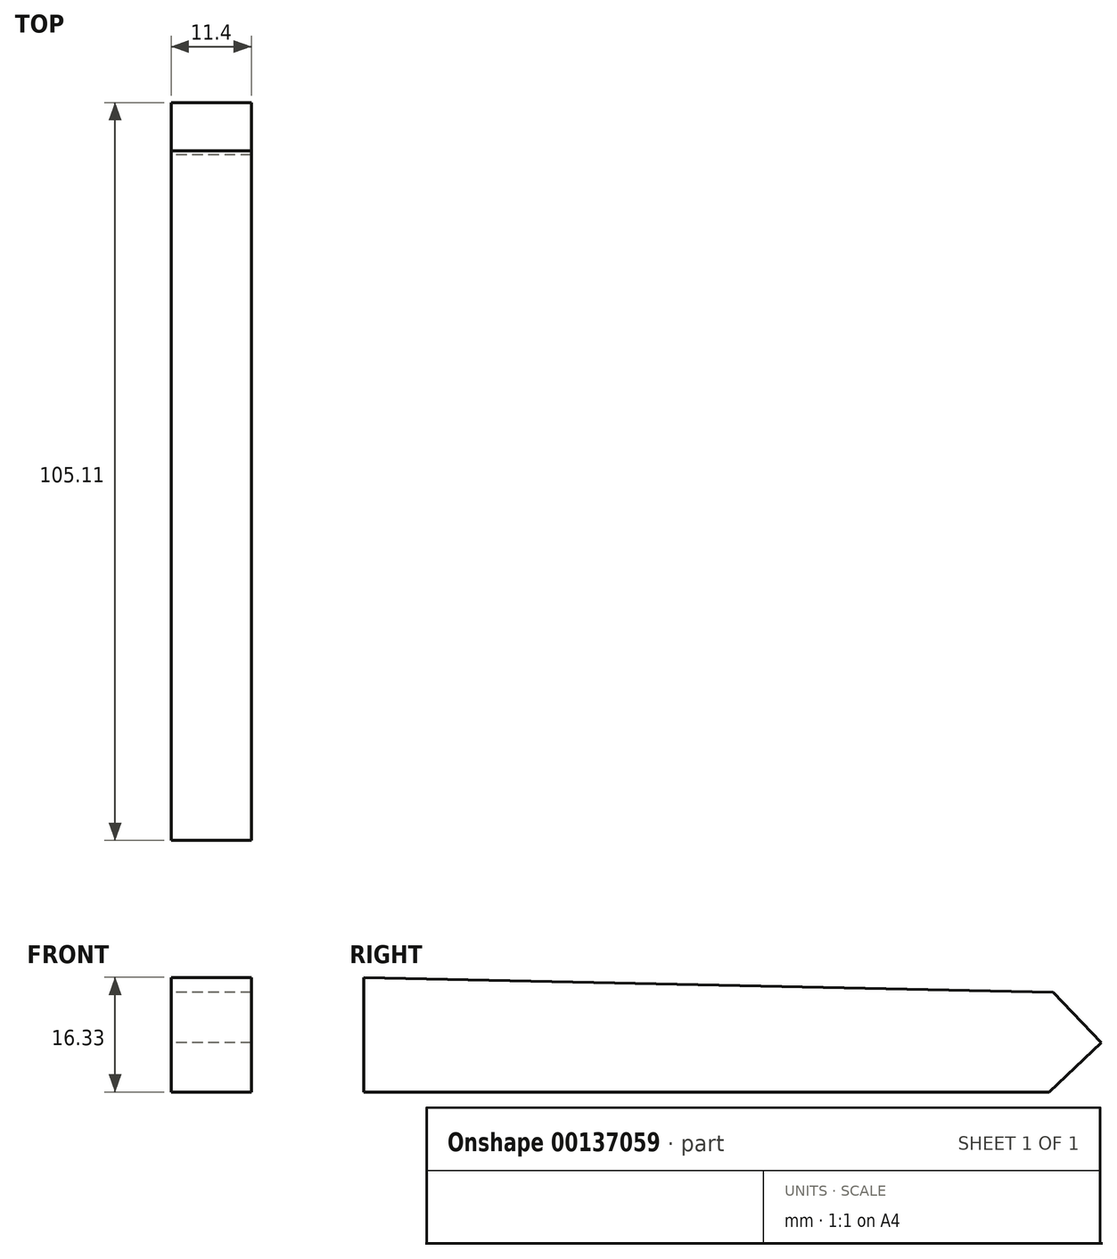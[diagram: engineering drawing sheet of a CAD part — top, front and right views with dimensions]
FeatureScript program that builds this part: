
annotation { "Feature Type Name" : "Feature", "Feature Type Description" : "" }
export const myFeature = defineFeature(function(context is Context, id is Id, definition is map)
    precondition{}
    {
        {
            var Q0;
            Q0=qCreatedBy(makeId("Right.planeOp"),FACE);
            var sketch = newSketch(context, id + "F0", { "sketchPlane" : qUnion([Q0])});
            skLineSegment(sketch, "E0", {"start": v(64.38, 7.22) * mm, "end": v(71.2, 0) * mm});
            skLineSegment(sketch, "E1", {"start": v(71.2, 0) * mm, "end": v(63.8, -7) * mm});
            skLineSegment(sketch, "E2", {"start": v(63.8, -7) * mm, "end": v(-33.9, -7) * mm});
            skLineSegment(sketch, "E3", {"start": v(-33.9, -7) * mm, "end": v(-33.9, 4.86) * mm});
            skLineSegment(sketch, "E4", {"start": v(-33.9, 4.86) * mm, "end": v(-33.9, 9.33) * mm});
            skLineSegment(sketch, "E5", {"start": v(-33.9, 9.33) * mm, "end": v(64.38, 7.22) * mm});
            skSolve(sketch);
        }
        {
            var Q0;
            Q0=makeQuery(id+"F0.imprint","IMPRINT",FACE,{"disambiguationData":[TD([[makeQuery(id+"F0.imprint","IMPRINT",EDGE,{"derivedFrom":sQuery(id+"F0.wireOp",EDGE,"E0")}),-1.0]])]});
            extrude(context, id + "F1", {"entities" : qUnion([Q0]), "depth" : 11.4 * mm});
        }
    });
